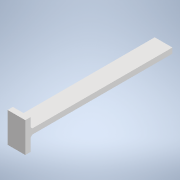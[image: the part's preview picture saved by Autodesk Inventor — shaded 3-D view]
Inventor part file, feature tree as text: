
AUTODESK INVENTOR PART (.ipt)
format: ipt  version: 2020 (Build 240168000, 168)  size: 118,784 bytes
history: native  units: mm
features: other x3, extrude x2, sketch x2, chamfer x1, reference x1, projected_geometry x1
ambient origin geometry x8: Origin, YZ Plane, XZ Plane, XY Plane, X Axis, Y Axis, Z Axis, Center Point
bodies: Solid1 (feature_tree)
feature tree (10):
  extrude  "Extrusion1"  Depth=8.0mm
  extrude  "Extrusion2"  Depth=3.0mm TaperAngle=0.0deg
  chamfer  "Chamfer1"  Distance=1.0mm Angle=45.0deg
  sketch  "Sketch1"  dims[d0=80.0mm d1=0.0mm d2=8.0mm]
  reference  "Reference1"
  sketch  "Sketch2"  dims[d3=6.0mm d4=3.0mm d5=0.0mm d6=1.0mm d7=2.0mm d8=45.0deg]
  projected_geometry  "Projected Loop1"
  parser-record x1  (decoder bookkeeping rows leaked as tree rows — omitted from the tree; the rows remain in map.json)
  other  "motorized2.iam"
  other  "servo_bracket:1"
note: 1 file-system path scrubbed to <path> (originals preserved in map.json)
